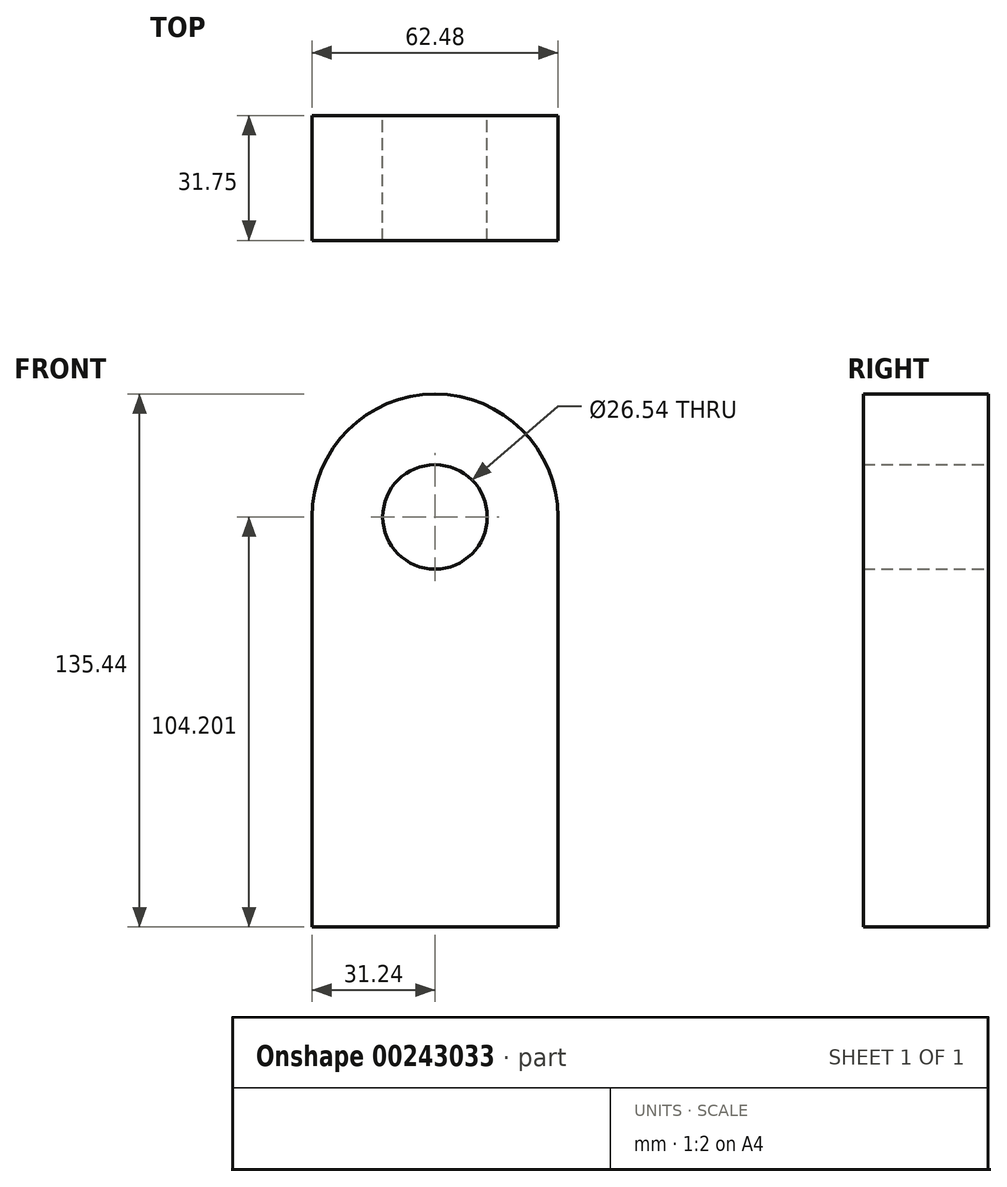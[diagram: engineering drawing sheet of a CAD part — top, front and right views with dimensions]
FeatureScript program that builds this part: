
annotation { "Feature Type Name" : "Feature", "Feature Type Description" : "" }
export const myFeature = defineFeature(function(context is Context, id is Id, definition is map)
    precondition{}
    {
        {
            var Q0;
            Q0=qCreatedBy(makeId("Front.planeOp"),FACE);
            var sketch = newSketch(context, id + "F0", { "sketchPlane" : qUnion([Q0])});
            skLineSegment(sketch, "E0.top", {"start": v(-31.24, -52.1) * mm, "end": v(31.24, -52.1) * mm});
            skLineSegment(sketch, "E0.left", {"start": v(-31.24, 52.1) * mm, "end": v(-31.24, -52.1) * mm});
            skLineSegment(sketch, "E0.right", {"start": v(31.24, 52.1) * mm, "end": v(31.24, -52.1) * mm});
            skPoint(sketch, "E0.middle", {"position": v(0, 0) * mm});
            skArc(sketch, "E1", {"start": v(31.24, 52.1) * mm, "mid": v(0, 83.34) * mm, "end": v(-31.24, 52.1) * mm});
            skCircle(sketch, "E2", {"center": v(0, 52.1) * mm, "radius": 13.27 * mm});
            skSolve(sketch);
        }
        {
            var Q0;
            Q0=makeQuery(id+"F0.imprint","IMPRINT",FACE,{"disambiguationData":[TD([[makeQuery(id+"F0.imprint","IMPRINT",EDGE,{"derivedFrom":sQuery(id+"F0.wireOp",EDGE,"E0.top")}),1.0]])]});
            extrude(context, id + "F1", {"entities" : qUnion([Q0]), "depth" : 31.75 * mm});
        }
    });
